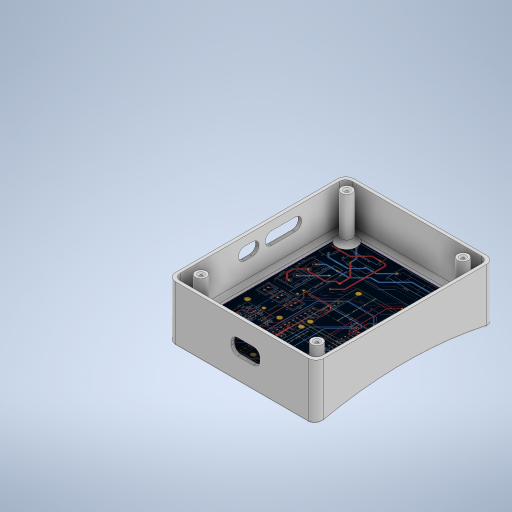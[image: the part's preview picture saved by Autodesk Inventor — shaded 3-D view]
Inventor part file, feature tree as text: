
AUTODESK INVENTOR PART (.ipt)
format: ipt  version: 2024.4 (Build 284460000, 460)  size: 1,009,664 bytes
history: native  units: mm
features: sketch x9, fillet x9, extrude x8, other x1
ambient origin geometry x8: Origin, YZ Plane, XZ Plane, XY Plane, X Axis, Y Axis, Z Axis, Center Point
bodies: Solid1 (feature_tree)
feature tree (27):
  sketch  "Sketch1"  dims[d28=4.0mm d29=2.0mm]
  extrude  "Extrusion1"  Depth=2.0mm
  extrude  "Extrusion2"  Depth=2.0mm
  extrude  "Extrusion3"  Depth=2.0mm TaperAngle=0.0deg
  extrude  "Extrusion4"  Depth=7.0mm
  fillet  "Fillet4"  Radius=7.0mm
  fillet  "Fillet5"  Radius=7.0mm
  extrude  "Extrusion5"  Depth=2.0mm
  extrude  "Extrusion6"  Depth=2.0mm
  fillet  "Fillet6"  Radius=2.0mm
  fillet  "Fillet7"  Radius=12.0mm
  fillet  "Fillet8"  Radius=3.0mm
  extrude  "Extrusion7"  Depth=7.0mm TaperAngle=0.0deg
  fillet  "Fillet10"  Radius=112.838mm
  fillet  "Fillet11"  Radius=240.0mm
  extrude  "Extrusion8"  Depth=5.0mm
  fillet  "Fillet12"  Radius=4.0mm
  fillet  "Fillet13"  Radius=5.0mm
  other  "Image3"
  sketch  "Sketch2"  dims[d30=4.0mm d31=2.0mm]
  sketch  "Sketch3"  dims[d32=26.5mm d33=0.0mm d34=2.0mm d35=0.0mm]
  sketch  "Sketch4"  dims[d38=7.0mm d39=7.0mm d40=7.0mm d41=7.0mm]
  sketch  "Sketch5"  dims[d42=28.0mm d43=0.0mm d45=2.0mm]
  sketch  "Sketch6"  dims[d46=2.0mm d47=2.0mm d48=2.0mm d49=12.0mm d50=0.0mm d51=3.0mm]
  sketch  "Sketch7"  dims[d52=2.3mm d53=7.0mm d54=0.0mm d56=112.838mm d57=240.0mm]
  sketch  "Sketch8"  dims[d58=20.0mm d59=0.0mm d60=5.0mm d61=4.0mm d62=5.0mm]
  sketch  "Sketch9"  dims[d63=5.0mm d64=5.0mm d65=5.0mm d66=1.0mm d67=15.0mm d68=0.0mm d70=8.0mm d71=40.0mm d72=3.0mm d73=4.0mm d74=25.0mm d76=4.0mm d80=13.0mm d81=23.0mm d82=26.5mm d83=0.0mm d84=4.0mm d85=10.0mm d86=18.0mm d87=40.5mm d90=12.5mm d91=1.0mm d92=7.0mm d93=7.0mm d96=94.030423mm d97=112.838mm d23=0.5mm d24=0.872665mm d25=0.5mm d26=0.872665mm d77=0.5mm d78=0.872665mm d79=0.5mm]
